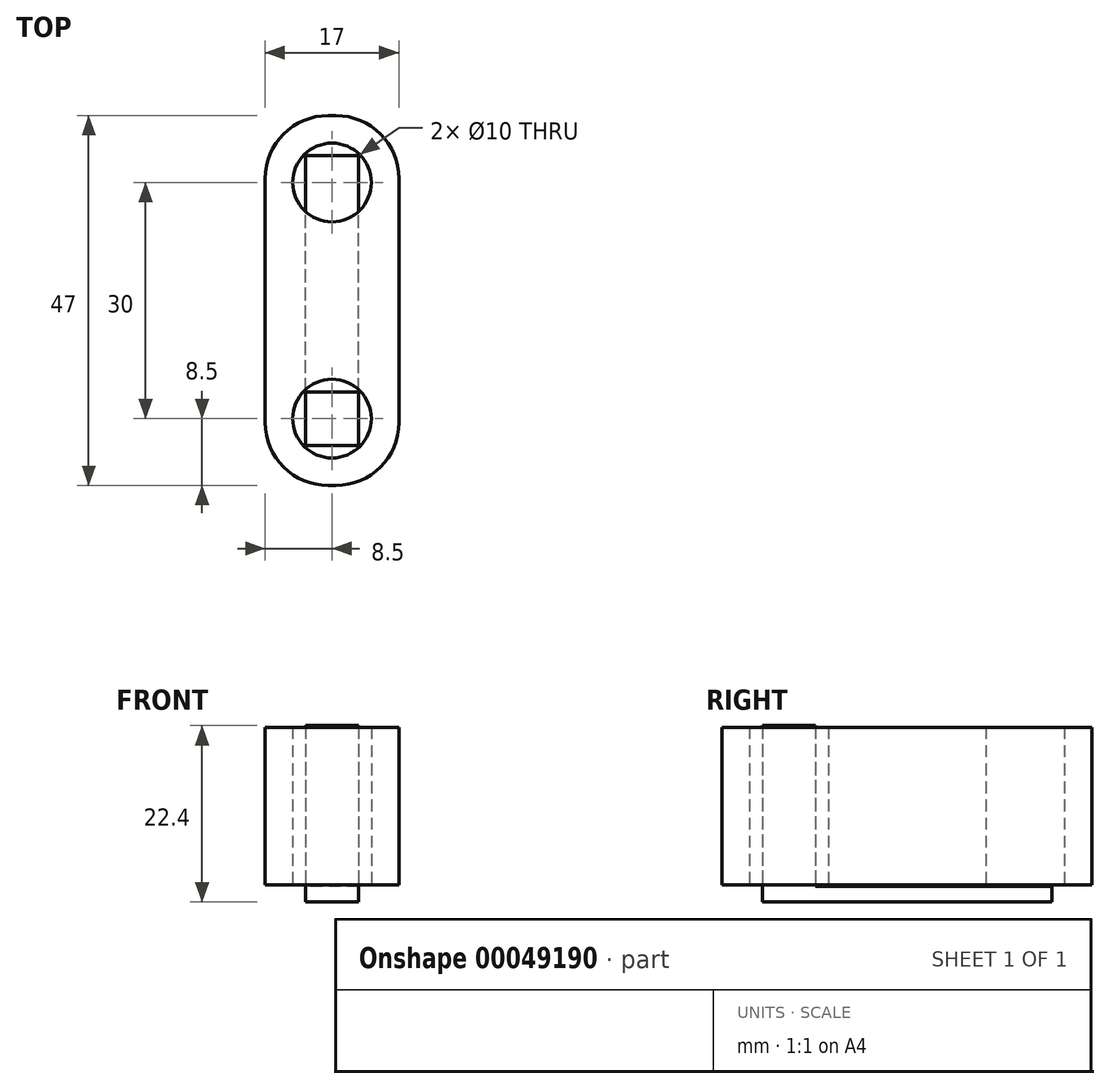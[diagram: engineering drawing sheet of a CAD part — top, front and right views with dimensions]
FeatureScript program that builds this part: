
annotation { "Feature Type Name" : "Feature", "Feature Type Description" : "" }
export const myFeature = defineFeature(function(context is Context, id is Id, definition is map)
    precondition{}
    {
        {
            var Q0;
            Q0=qCreatedBy(makeId("Top.planeOp"),FACE);
            var sketch = newSketch(context, id + "F0", { "sketchPlane" : qUnion([Q0])});
            skCircle(sketch, "E0", {"center": v(0, 0) * mm, "radius": 5 * mm});
            skCircle(sketch, "E1", {"center": v(0, 30) * mm, "radius": 5 * mm});
            skLineSegment(sketch, "E2.rect.bottom", {"start": v(8.5, 38.5) * mm, "end": v(-8.5, 38.5) * mm});
            skLineSegment(sketch, "E2.rect.top", {"start": v(8.5, -8.5) * mm, "end": v(-8.5, -8.5) * mm});
            skLineSegment(sketch, "E2.rect.left", {"start": v(8.5, 38.5) * mm, "end": v(8.5, -8.5) * mm});
            skLineSegment(sketch, "E2.rect.right", {"start": v(-8.5, 38.5) * mm, "end": v(-8.5, -8.5) * mm});
            skPoint(sketch, "E2.rect.middle", {"position": v(0, 15) * mm});
            skLineSegment(sketch, "E3", {"start": v(0, 30) * mm, "end": v(0, 0) * mm, "construction": true});
            skSolve(sketch);
        }
        {
            var Q0;
            Q0=makeQuery(id+"F0.imprint","IMPRINT",FACE,{"disambiguationData":[TD([[makeQuery(id+"F0.imprint","IMPRINT",EDGE,{"derivedFrom":sQuery(id+"F0.wireOp",EDGE,"E0")}),-1.0]])]});
            extrude(context, id + "F1", {"entities" : qUnion([Q0]), "depth" : 20 * mm});
        }
        {
            var Q0;
            Q0=makeQuery(id+"F1.opExtrude","SWEPT_EDGE",EDGE,{"disambiguationData":[OSD([sQuery(id+"F0.wireOp",EDGE,"E2.rect.top"),sQuery(id+"F0.wireOp",EDGE,"E2.rect.left")])]});
            var Q1;
            Q1=makeQuery(id+"F1.opExtrude","SWEPT_EDGE",EDGE,{"disambiguationData":[OSD([sQuery(id+"F0.wireOp",EDGE,"E2.rect.top"),sQuery(id+"F0.wireOp",EDGE,"E2.rect.right")])]});
            var Q2;
            Q2=makeQuery(id+"F1.opExtrude","SWEPT_EDGE",EDGE,{"disambiguationData":[OSD([sQuery(id+"F0.wireOp",EDGE,"E2.rect.bottom"),sQuery(id+"F0.wireOp",EDGE,"E2.rect.left")])]});
            var Q3;
            Q3=makeQuery(id+"F1.opExtrude","SWEPT_EDGE",EDGE,{"disambiguationData":[OSD([sQuery(id+"F0.wireOp",EDGE,"E2.rect.bottom"),sQuery(id+"F0.wireOp",EDGE,"E2.rect.right")])]});
            fillet(context, id + "F2", {"entities" : qUnion([Q0, Q1, Q2, Q3]), "radius" : 8 * mm, "tangentPropagation" : true, "allowEdgeOverflow" : false});
        }
        {
            var Q0;
            Q0=qCreatedBy(makeId("Top.planeOp"),FACE);
            cPlane(context, id + "F3", {"entities" : qUnion([Q0]), "cplaneType" : CPlaneType.OFFSET, "offset" : .2 * mm, "oppositeDirection" : true, "width" : 150 * mm, "height" : 150 * mm});
        }
        {
            var Q0;
            Q0=qCreatedBy(id+"F3.planeOp",FACE);
            var sketch = newSketch(context, id + "F4", { "sketchPlane" : qUnion([Q0])});
            skLineSegment(sketch, "E4.rect.bottom", {"start": v(3.4, -3.4) * mm, "end": v(-3.4, -3.4) * mm});
            skLineSegment(sketch, "E4.rect.top", {"start": v(3.4, 3.4) * mm, "end": v(-3.4, 3.4) * mm});
            skLineSegment(sketch, "E4.rect.left", {"start": v(3.4, -3.4) * mm, "end": v(3.4, 3.4) * mm});
            skLineSegment(sketch, "E4.rect.right", {"start": v(-3.4, -3.4) * mm, "end": v(-3.4, 3.4) * mm});
            skPoint(sketch, "E4.rect.middle", {"position": v(0, 0) * mm});
            skCircle(sketch, "E5", {"center": v(0, 0) * mm, "radius": 4.8 * mm, "construction": true});
            skLineSegment(sketch, "E6.bottom", {"start": v(3.4, -3.4) * mm, "end": v(1.4, -3.4) * mm, "construction": true});
            skLineSegment(sketch, "E6.top", {"start": v(3.4, 33.4) * mm, "end": v(1.4, 33.4) * mm, "construction": true});
            skLineSegment(sketch, "E6.left", {"start": v(3.4, -3.4) * mm, "end": v(3.4, 33.4) * mm, "construction": true});
            skLineSegment(sketch, "E6.right", {"start": v(1.4, -3.4) * mm, "end": v(1.4, 33.4) * mm, "construction": true});
            skSolve(sketch);
        }
        {
            var Q0;
            Q0 = qSketchRegion(id + "F4", true);
            extrude(context, id + "F5", {"entities" : qUnion([Q0]), "depth" : 27 * mm - 6.6 * mm});
        }
        {
            var Q0;
            Q0=makeQuery(id+"F5.opExtrude","CAP_FACE",FACE,{"disambiguationData":[OSD([sQuery(id+"F4.wireOp",EDGE,"E4.rect.bottom"),sQuery(id+"F4.wireOp",EDGE,"E4.rect.top"),sQuery(id+"F4.wireOp",EDGE,"E4.rect.left"),sQuery(id+"F4.wireOp",EDGE,"E4.rect.right")])],"isStart":true});
            var sketch = newSketch(context, id + "F6", { "sketchPlane" : qUnion([Q0])});
            skLineSegment(sketch, "E7.bottom", {"start": v(3.4, 3.4) * mm, "end": v(-3.4, 3.4) * mm});
            skLineSegment(sketch, "E7.top", {"start": v(3.4, -33.4) * mm, "end": v(-3.4, -33.4) * mm});
            skLineSegment(sketch, "E7.left", {"start": v(3.4, 3.4) * mm, "end": v(3.4, -33.4) * mm});
            skLineSegment(sketch, "E7.right", {"start": v(-3.4, 3.4) * mm, "end": v(-3.4, -33.4) * mm});
            skSolve(sketch);
        }
        {
            var Q0;
            Q0 = qSketchRegion(id + "F6", true);
            extrude(context, id + "F7", {"entities" : qUnion([Q0]), "operationType" : NewBodyOperationType.ADD, "depth" : 2 * mm});
        }
    });
